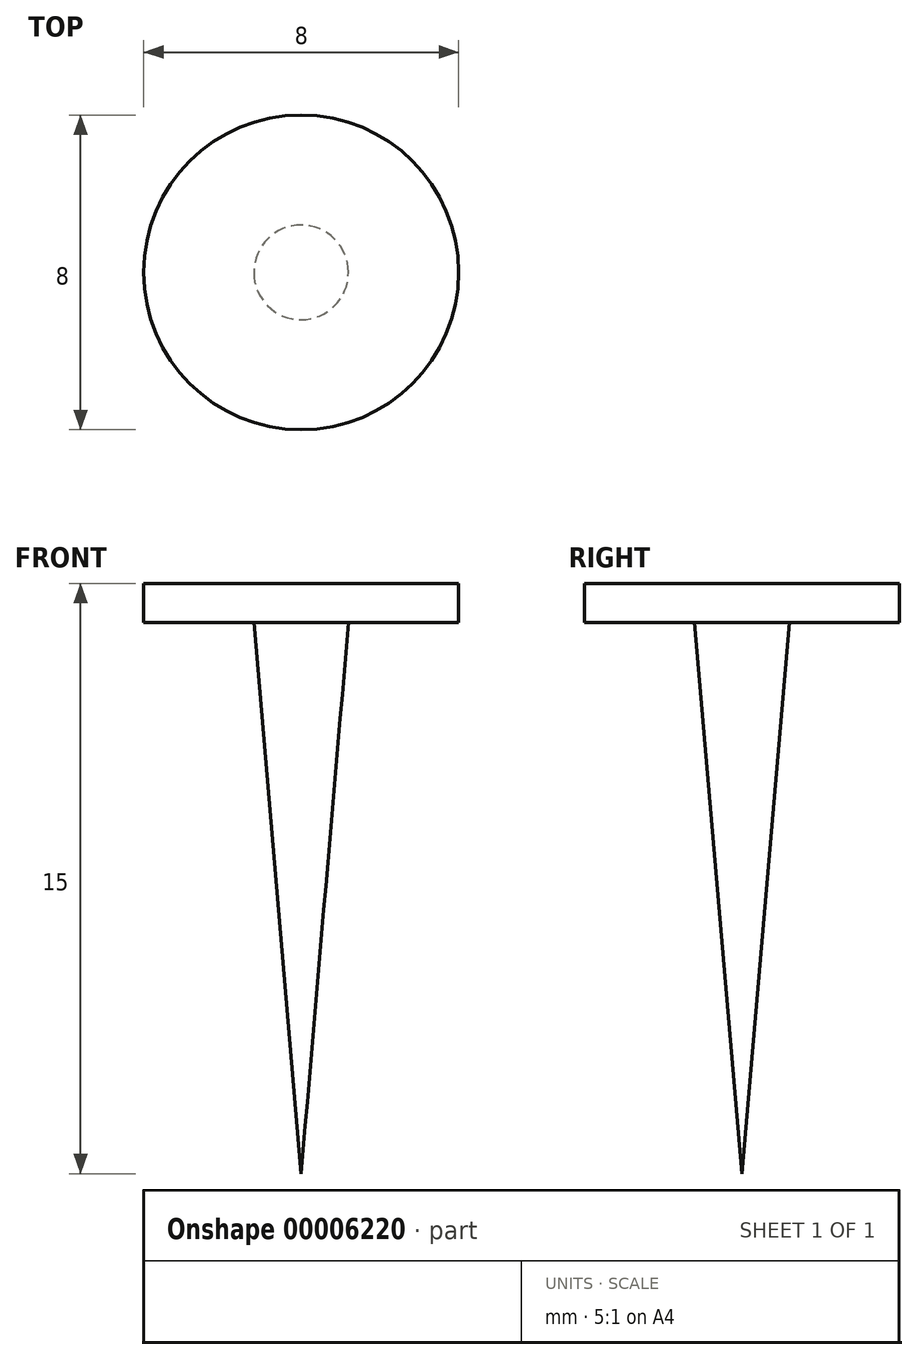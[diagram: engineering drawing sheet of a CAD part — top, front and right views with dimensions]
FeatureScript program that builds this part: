
annotation { "Feature Type Name" : "Feature", "Feature Type Description" : "" }
export const myFeature = defineFeature(function(context is Context, id is Id, definition is map)
    precondition{}
    {
        {
            var Q0;
            Q0=qCreatedBy(makeId("Front.planeOp"),FACE);
            var sketch = newSketch(context, id + "F0", { "sketchPlane" : qUnion([Q0])});
            skLineSegment(sketch, "E0", {"start": v(0, 0) * mm, "end": v(0, 14) * mm});
            skLineSegment(sketch, "E1.rect.bottom", {"start": v(4, 14) * mm, "end": v(0, 14) * mm});
            skLineSegment(sketch, "E1.rect.top", {"start": v(4, 15) * mm, "end": v(0, 15) * mm});
            skLineSegment(sketch, "E1.rect.left", {"start": v(4, 14) * mm, "end": v(4, 15) * mm});
            skPoint(sketch, "E1.rect.middle", {"position": v(0, 14.5) * mm});
            skPoint(sketch, "E2.orphan", {"position": v(-58.95, 14.5) * mm});
            skLineSegment(sketch, "E3", {"start": v(0, 0) * mm, "end": v(1.2, 14) * mm});
            skLineSegment(sketch, "E4", {"start": v(0, 14) * mm, "end": v(0, 15) * mm});
            skPoint(sketch, "E1.rect.right.end.orphan", {"position": v(-4, 15) * mm});
            skPoint(sketch, "E1.rect.right.start.orphan", {"position": v(-4, 14) * mm});
            skSolve(sketch);
        }
        {
            var Q0;
            Q0 = qSketchRegion(id + "F0", true);
            var Q1;
            Q1=sQuery(id+"F0.wireOp",EDGE,"E0");
            revolve(context, id + "F1", {"entities" : qUnion([Q0]), "axis" : qUnion([Q1]), "revolveType" : RevolveType.FULL});
        }
    });
